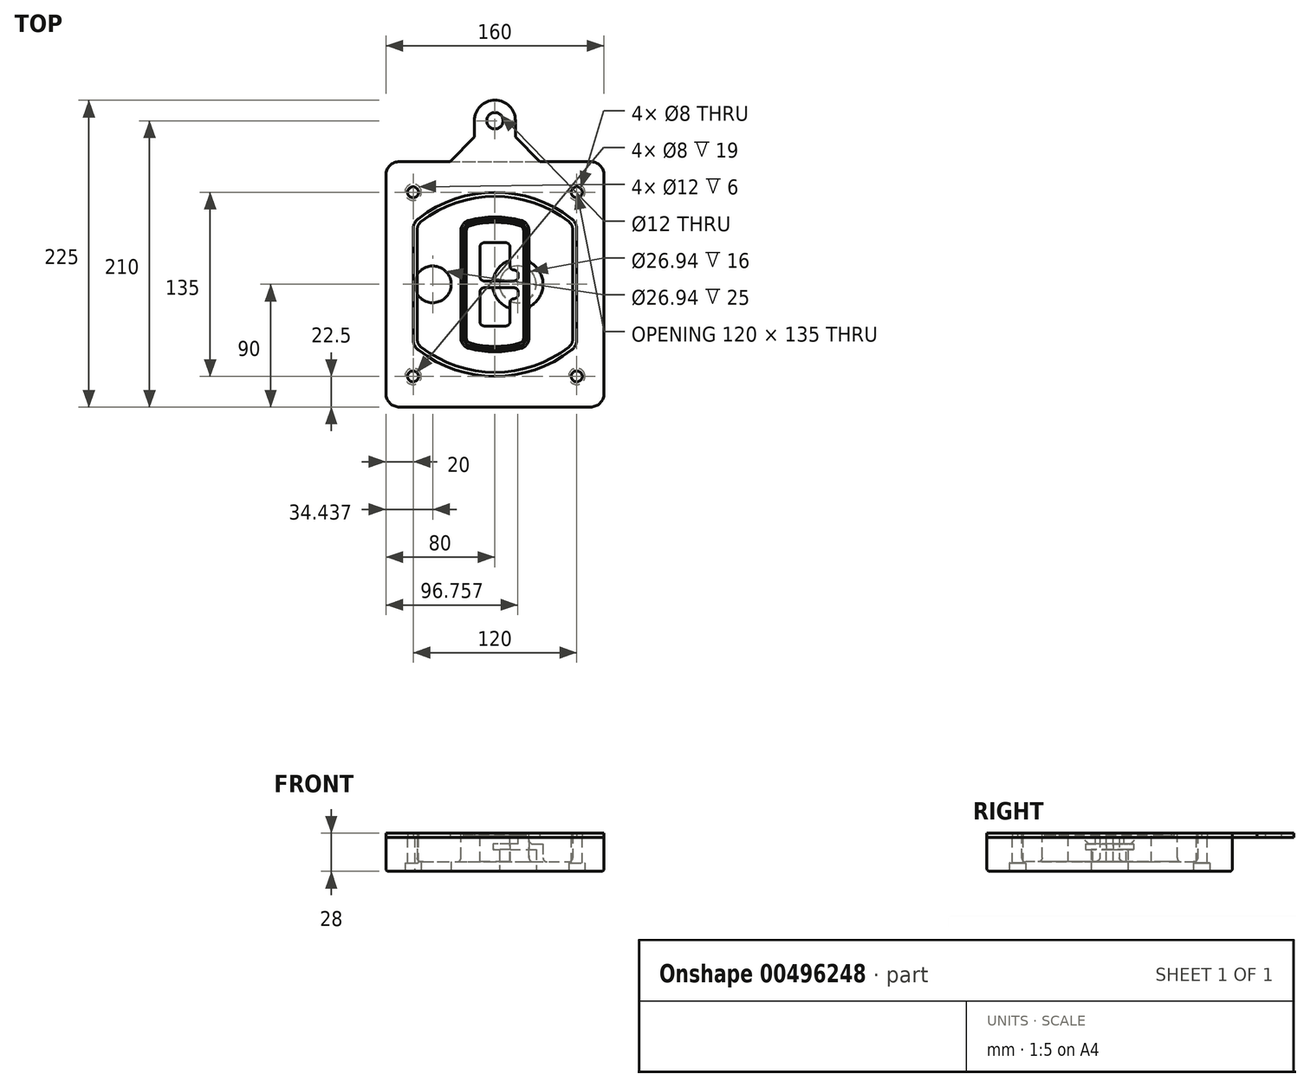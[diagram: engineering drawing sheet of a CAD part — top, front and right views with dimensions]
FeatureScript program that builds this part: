
annotation { "Feature Type Name" : "Feature", "Feature Type Description" : "" }
export const myFeature = defineFeature(function(context is Context, id is Id, definition is map)
    precondition{}
    {
        {
            var Q0;
            Q0=qCreatedBy(makeId("Top.planeOp"),FACE);
            var sketch = newSketch(context, id + "F0", { "sketchPlane" : qUnion([Q0])});
            skPoint(sketch, "E0.rect.middle", {"position": v(0, 0) * mm});
            skLineSegment(sketch, "E1.bottom", {"start": v(-70, -90) * mm, "end": v(70, -90) * mm});
            skLineSegment(sketch, "E1.top", {"start": v(-70, 90) * mm, "end": v(70, 90) * mm});
            skLineSegment(sketch, "E1.left", {"start": v(-80, -80) * mm, "end": v(-80, 80) * mm});
            skLineSegment(sketch, "E1.right", {"start": v(80, -80) * mm, "end": v(80, 80) * mm});
            skLineSegment(sketch, "E2", {"start": v(-80, 90) * mm, "end": v(80, -90) * mm, "construction": true});
            skLineSegment(sketch, "E3", {"start": v(80, 90) * mm, "end": v(-80, -90) * mm, "construction": true});
            skCircle(sketch, "E4", {"center": v(-60, 67.5) * mm, "radius": 4 * mm});
            skCircle(sketch, "E5", {"center": v(60, 67.5) * mm, "radius": 4 * mm});
            skCircle(sketch, "E6", {"center": v(60, -67.5) * mm, "radius": 4 * mm});
            skCircle(sketch, "E7", {"center": v(-60, -67.5) * mm, "radius": 4 * mm});
            skLineSegment(sketch, "E8", {"start": v(-60, 67.5) * mm, "end": v(60, 67.5) * mm, "construction": true});
            skLineSegment(sketch, "E9", {"start": v(60, 67.5) * mm, "end": v(60, -67.5) * mm, "construction": true});
            skLineSegment(sketch, "E10", {"start": v(60, -67.5) * mm, "end": v(-60, -67.5) * mm, "construction": true});
            skLineSegment(sketch, "E11", {"start": v(-60, -67.5) * mm, "end": v(-60, 67.5) * mm, "construction": true});
            skLineSegment(sketch, "E12", {"start": v(-60, 40.3) * mm, "end": v(-60, -40.3) * mm});
            skLineSegment(sketch, "E13", {"start": v(60, 40.3) * mm, "end": v(60, -40.3) * mm});
            skArc(sketch, "E14", {"start": v(56.15, 48.18) * mm, "mid": v(0, 67.5) * mm, "end": v(-56.15, 48.18) * mm});
            skArc(sketch, "E15", {"start": v(-56.15, -48.18) * mm, "mid": v(0, -67.5) * mm, "end": v(56.15, -48.18) * mm});
            skLineSegment(sketch, "E16", {"start": v(-60, 0) * mm, "end": v(60, 0) * mm, "construction": true});
            skPoint(sketch, "E17.visualSharp", {"position": v(-60, -45) * mm});
            skArc(sketch, "E17.filletArc", {"start": v(-60, -40.3) * mm, "mid": v(-58.99, -44.68) * mm, "end": v(-56.15, -48.18) * mm});
            skPoint(sketch, "E18.visualSharp", {"position": v(-60, 45) * mm});
            skArc(sketch, "E18.filletArc", {"start": v(-56.15, 48.18) * mm, "mid": v(-58.99, 44.68) * mm, "end": v(-60, 40.3) * mm});
            skPoint(sketch, "E19.visualSharp", {"position": v(60, 45) * mm});
            skArc(sketch, "E19.filletArc", {"start": v(60, 40.3) * mm, "mid": v(58.99, 44.68) * mm, "end": v(56.15, 48.18) * mm});
            skPoint(sketch, "E20.visualSharp", {"position": v(60, -45) * mm});
            skArc(sketch, "E20.filletArc", {"start": v(56.15, -48.18) * mm, "mid": v(58.99, -44.68) * mm, "end": v(60, -40.3) * mm});
            skPoint(sketch, "E21.visualSharp", {"position": v(-80, 90) * mm});
            skArc(sketch, "E21.filletArc", {"start": v(-70, 90) * mm, "mid": v(-77.07, 87.07) * mm, "end": v(-80, 80) * mm});
            skPoint(sketch, "E22.visualSharp", {"position": v(80, 90) * mm});
            skArc(sketch, "E22.filletArc", {"start": v(80, 80) * mm, "mid": v(77.07, 87.07) * mm, "end": v(70, 90) * mm});
            skPoint(sketch, "E23.visualSharp", {"position": v(80, -90) * mm});
            skArc(sketch, "E23.filletArc", {"start": v(70, -90) * mm, "mid": v(77.07, -87.07) * mm, "end": v(80, -80) * mm});
            skPoint(sketch, "E24.visualSharp", {"position": v(-80, -90) * mm});
            skArc(sketch, "E24.filletArc", {"start": v(-80, -80) * mm, "mid": v(-77.07, -87.07) * mm, "end": v(-70, -90) * mm});
            skArc(sketch, "E25.0", {"start": v(57, 40.3) * mm, "mid": v(56.3, 43.36) * mm, "end": v(54.3, 45.81) * mm});
            skLineSegment(sketch, "E25.1", {"start": v(57, 40.3) * mm, "end": v(57, -40.3) * mm});
            skArc(sketch, "E25.2", {"start": v(54.3, -45.81) * mm, "mid": v(56.3, -43.36) * mm, "end": v(57, -40.3) * mm});
            skArc(sketch, "E25.3", {"start": v(-54.3, -45.81) * mm, "mid": v(0, -64.5) * mm, "end": v(54.3, -45.81) * mm});
            skArc(sketch, "E25.4", {"start": v(-57, -40.3) * mm, "mid": v(-56.3, -43.36) * mm, "end": v(-54.3, -45.81) * mm});
            skArc(sketch, "E25.5", {"start": v(54.3, 45.81) * mm, "mid": v(0, 64.5) * mm, "end": v(-54.3, 45.81) * mm});
            skLineSegment(sketch, "E25.6", {"start": v(-57, 40.3) * mm, "end": v(-57, -40.3) * mm});
            skArc(sketch, "E25.7", {"start": v(-54.3, 45.81) * mm, "mid": v(-56.3, 43.36) * mm, "end": v(-57, 40.3) * mm});
            skArc(sketch, "E26.0", {"start": v(-58.62, 51.33) * mm, "mid": v(-62.58, 46.43) * mm, "end": v(-64, 40.3) * mm});
            skArc(sketch, "E26.1", {"start": v(58.62, 51.33) * mm, "mid": v(0, 71.5) * mm, "end": v(-58.62, 51.33) * mm});
            skArc(sketch, "E26.2", {"start": v(64, 40.3) * mm, "mid": v(62.58, 46.43) * mm, "end": v(58.62, 51.33) * mm});
            skLineSegment(sketch, "E26.3", {"start": v(64, 40.3) * mm, "end": v(64, -40.3) * mm});
            skArc(sketch, "E26.4", {"start": v(58.62, -51.33) * mm, "mid": v(62.58, -46.43) * mm, "end": v(64, -40.3) * mm});
            skLineSegment(sketch, "E26.5", {"start": v(-64, 40.3) * mm, "end": v(-64, -40.3) * mm});
            skArc(sketch, "E26.6", {"start": v(-58.62, -51.33) * mm, "mid": v(0, -71.5) * mm, "end": v(58.62, -51.33) * mm});
            skArc(sketch, "E26.7", {"start": v(-64, -40.3) * mm, "mid": v(-62.58, -46.43) * mm, "end": v(-58.62, -51.33) * mm});
            skSolve(sketch);
        }
        {
            var Q0;
            Q0=makeQuery(id+"F0.imprint","IMPRINT",FACE,{"disambiguationData":[TD([[makeQuery(id+"F0.imprint","IMPRINT",EDGE,{"derivedFrom":sQuery(id+"F0.wireOp",EDGE,"E1.bottom")}),1.0]])]});
            var Q1;
            Q1=makeQuery(id+"F0.imprint","IMPRINT",FACE,{"disambiguationData":[TD([[makeQuery(id+"F0.imprint","IMPRINT",EDGE,{"derivedFrom":sQuery(id+"F0.wireOp",EDGE,"E12")}),1.0]])]});
            var Q2;
            Q2=makeQuery(id+"F0.imprint","IMPRINT",FACE,{"disambiguationData":[TD([[makeQuery(id+"F0.imprint","IMPRINT",EDGE,{"derivedFrom":sQuery(id+"F0.wireOp",EDGE,"E25.0")}),1.0]])]});
            var Q3;
            Q3=makeQuery(id+"F0.imprint","IMPRINT",FACE,{"disambiguationData":[TD([[makeQuery(id+"F0.imprint","IMPRINT",EDGE,{"derivedFrom":sQuery(id+"F0.wireOp",EDGE,"E12")}),-1.0]])]});
            extrude(context, id + "F1", {"entities" : qUnion([Q0, Q1, Q2, Q3]), "oppositeDirection" : true, "depth" : 25 * mm});
        }
        {
            var Q0;
            Q0=makeQuery(id+"F0.imprint","IMPRINT",FACE,{"disambiguationData":[TD([[makeQuery(id+"F0.imprint","IMPRINT",EDGE,{"derivedFrom":sQuery(id+"F0.wireOp",EDGE,"E12")}),1.0]])]});
            extrude(context, id + "F2", {"entities" : qUnion([Q0]), "operationType" : NewBodyOperationType.ADD, "depth" : 3 * mm});
        }
        {
            var Q0;
            Q0=makeQuery(id+"F0.imprint","IMPRINT",FACE,{"disambiguationData":[TD([[makeQuery(id+"F0.imprint","IMPRINT",EDGE,{"derivedFrom":sQuery(id+"F0.wireOp",EDGE,"E25.0")}),1.0]])]});
            extrude(context, id + "F3", {"entities" : qUnion([Q0]), "operationType" : NewBodyOperationType.REMOVE, "oppositeDirection" : true, "depth" : 18 * mm});
        }
        {
            var Q0;
            Q0=makeQuery(id+"F2.opExtrude","CAP_FACE",FACE,{"disambiguationData":[OSD([sQuery(id+"F0.wireOp",EDGE,"E12"),sQuery(id+"F0.wireOp",EDGE,"E13"),sQuery(id+"F0.wireOp",EDGE,"E14"),sQuery(id+"F0.wireOp",EDGE,"E15"),sQuery(id+"F0.wireOp",EDGE,"E17.filletArc"),sQuery(id+"F0.wireOp",EDGE,"E18.filletArc"),sQuery(id+"F0.wireOp",EDGE,"E19.filletArc"),sQuery(id+"F0.wireOp",EDGE,"E20.filletArc"),sQuery(id+"F0.wireOp",EDGE,"E25.0"),sQuery(id+"F0.wireOp",EDGE,"E25.1"),sQuery(id+"F0.wireOp",EDGE,"E25.2"),sQuery(id+"F0.wireOp",EDGE,"E25.3"),sQuery(id+"F0.wireOp",EDGE,"E25.4"),sQuery(id+"F0.wireOp",EDGE,"E25.5"),sQuery(id+"F0.wireOp",EDGE,"E25.6"),sQuery(id+"F0.wireOp",EDGE,"E25.7")])],"isStart":false});
            var sketch = newSketch(context, id + "F4", { "sketchPlane" : qUnion([Q0])});
            skArc(sketch, "E27.0", {"start": v(-19.08, -46.97) * mm, "mid": v(0, -49.5) * mm, "end": v(19.08, -46.97) * mm});
            skArc(sketch, "E28.0", {"start": v(19.08, 46.97) * mm, "mid": v(0, 49.5) * mm, "end": v(-19.08, 46.97) * mm});
            skLineSegment(sketch, "E29", {"start": v(-25, 39.25) * mm, "end": v(-25, -39.25) * mm});
            skLineSegment(sketch, "E30", {"start": v(25, 39.25) * mm, "end": v(25, -39.25) * mm});
            skLineSegment(sketch, "E31", {"start": v(-25, 45.1) * mm, "end": v(25, 45.1) * mm, "construction": true});
            skLineSegment(sketch, "E32", {"start": v(-25, -45.1) * mm, "end": v(25, -45.1) * mm, "construction": true});
            skPoint(sketch, "E33.visualSharp", {"position": v(-25, 45.1) * mm});
            skArc(sketch, "E33.filletArc", {"start": v(-19.08, 46.97) * mm, "mid": v(-23.35, 44.11) * mm, "end": v(-25, 39.25) * mm});
            skPoint(sketch, "E34.visualSharp", {"position": v(25, 45.1) * mm});
            skArc(sketch, "E34.filletArc", {"start": v(25, 39.25) * mm, "mid": v(23.35, 44.11) * mm, "end": v(19.08, 46.97) * mm});
            skPoint(sketch, "E35.visualSharp", {"position": v(25, -45.1) * mm});
            skArc(sketch, "E35.filletArc", {"start": v(19.08, -46.97) * mm, "mid": v(23.35, -44.11) * mm, "end": v(25, -39.25) * mm});
            skPoint(sketch, "E36.visualSharp", {"position": v(-25, -45.1) * mm});
            skArc(sketch, "E36.filletArc", {"start": v(-25, -39.25) * mm, "mid": v(-23.35, -44.11) * mm, "end": v(-19.08, -46.97) * mm});
            skArc(sketch, "E37.0", {"start": v(54.3, 45.81) * mm, "mid": v(0, 64.5) * mm, "end": v(-54.3, 45.81) * mm});
            skArc(sketch, "E37.1", {"start": v(-54.3, 45.81) * mm, "mid": v(-56.3, 43.36) * mm, "end": v(-57, 40.3) * mm});
            skLineSegment(sketch, "E37.2", {"start": v(-57, 40.3) * mm, "end": v(-57, -40.3) * mm});
            skArc(sketch, "E37.3", {"start": v(-57, -40.3) * mm, "mid": v(-56.3, -43.36) * mm, "end": v(-54.3, -45.81) * mm});
            skArc(sketch, "E37.4", {"start": v(-54.3, -45.81) * mm, "mid": v(0, -64.5) * mm, "end": v(54.3, -45.81) * mm});
            skArc(sketch, "E37.5", {"start": v(54.3, -45.81) * mm, "mid": v(56.3, -43.36) * mm, "end": v(57, -40.3) * mm});
            skLineSegment(sketch, "E37.6", {"start": v(57, 40.3) * mm, "end": v(57, -40.3) * mm});
            skArc(sketch, "E37.7", {"start": v(57, 40.3) * mm, "mid": v(56.3, 43.36) * mm, "end": v(54.3, 45.81) * mm});
            skLineSegment(sketch, "E38.0", {"start": v(23, 39.25) * mm, "end": v(23, -39.25) * mm});
            skArc(sketch, "E38.1", {"start": v(18.56, -45.04) * mm, "mid": v(21.76, -42.9) * mm, "end": v(23, -39.25) * mm});
            skArc(sketch, "E38.2", {"start": v(-18.56, -45.04) * mm, "mid": v(0, -47.5) * mm, "end": v(18.56, -45.04) * mm});
            skArc(sketch, "E38.3", {"start": v(-23, -39.25) * mm, "mid": v(-21.76, -42.9) * mm, "end": v(-18.56, -45.04) * mm});
            skLineSegment(sketch, "E38.4", {"start": v(-23, 39.25) * mm, "end": v(-23, -39.25) * mm});
            skArc(sketch, "E38.5", {"start": v(23, 39.25) * mm, "mid": v(21.76, 42.9) * mm, "end": v(18.56, 45.04) * mm});
            skArc(sketch, "E38.6", {"start": v(-18.56, 45.04) * mm, "mid": v(-21.76, 42.9) * mm, "end": v(-23, 39.25) * mm});
            skArc(sketch, "E38.7", {"start": v(18.56, 45.04) * mm, "mid": v(0, 47.5) * mm, "end": v(-18.56, 45.04) * mm});
            skArc(sketch, "E39.0", {"start": v(21, 39.25) * mm, "mid": v(20.18, 41.68) * mm, "end": v(18.04, 43.1) * mm});
            skLineSegment(sketch, "E39.1", {"start": v(21, 39.25) * mm, "end": v(21, -39.25) * mm});
            skArc(sketch, "E39.2", {"start": v(18.04, -43.1) * mm, "mid": v(20.18, -41.68) * mm, "end": v(21, -39.25) * mm});
            skArc(sketch, "E39.3", {"start": v(-18.04, -43.1) * mm, "mid": v(0, -45.5) * mm, "end": v(18.04, -43.1) * mm});
            skArc(sketch, "E39.4", {"start": v(-21, -39.25) * mm, "mid": v(-20.18, -41.68) * mm, "end": v(-18.04, -43.1) * mm});
            skArc(sketch, "E39.5", {"start": v(18.04, 43.1) * mm, "mid": v(0, 45.5) * mm, "end": v(-18.04, 43.1) * mm});
            skLineSegment(sketch, "E39.6", {"start": v(-21, 39.25) * mm, "end": v(-21, -39.25) * mm});
            skArc(sketch, "E39.7", {"start": v(-18.04, 43.1) * mm, "mid": v(-20.18, 41.68) * mm, "end": v(-21, 39.25) * mm});
            skLineSegment(sketch, "E40", {"start": v(-25, 0) * mm, "end": v(25, 0) * mm, "construction": true});
            skLineSegment(sketch, "E41", {"start": v(-11, 5.5) * mm, "end": v(-11, 27.5) * mm});
            skLineSegment(sketch, "E42", {"start": v(-8, 30.5) * mm, "end": v(8, 30.5) * mm});
            skLineSegment(sketch, "E43", {"start": v(11, 27.5) * mm, "end": v(11, 13.5) * mm});
            skLineSegment(sketch, "E44", {"start": v(14, 10.5) * mm, "end": v(14, 10.5) * mm});
            skLineSegment(sketch, "E45", {"start": v(17, 7.5) * mm, "end": v(17, 5.5) * mm});
            skLineSegment(sketch, "E46", {"start": v(14, 2.5) * mm, "end": v(-8, 2.5) * mm});
            skPoint(sketch, "E47.visualSharp", {"position": v(-11, 30.5) * mm});
            skArc(sketch, "E47.filletArc", {"start": v(-8, 30.5) * mm, "mid": v(-10.12, 29.62) * mm, "end": v(-11, 27.5) * mm});
            skPoint(sketch, "E48.visualSharp", {"position": v(11, 30.5) * mm});
            skArc(sketch, "E48.filletArc", {"start": v(11, 27.5) * mm, "mid": v(10.12, 29.62) * mm, "end": v(8, 30.5) * mm});
            skPoint(sketch, "E49.visualSharp", {"position": v(11, 10.5) * mm});
            skArc(sketch, "E49.filletArc", {"start": v(11, 13.5) * mm, "mid": v(11.88, 11.38) * mm, "end": v(14, 10.5) * mm});
            skPoint(sketch, "E50.visualSharp", {"position": v(17, 10.5) * mm});
            skArc(sketch, "E50.filletArc", {"start": v(17, 7.5) * mm, "mid": v(16.12, 9.62) * mm, "end": v(14, 10.5) * mm});
            skPoint(sketch, "E51.visualSharp", {"position": v(17, 2.5) * mm});
            skArc(sketch, "E51.filletArc", {"start": v(14, 2.5) * mm, "mid": v(16.12, 3.38) * mm, "end": v(17, 5.5) * mm});
            skPoint(sketch, "E52.visualSharp", {"position": v(-11, 2.5) * mm});
            skArc(sketch, "E52.filletArc", {"start": v(-11, 5.5) * mm, "mid": v(-10.12, 3.38) * mm, "end": v(-8, 2.5) * mm});
            skLineSegment(sketch, "E53.0.MirrorCS", {"start": v(14, -2.5) * mm, "end": v(-8, -2.5) * mm});
            skArc(sketch, "E54.0.MirrorCS", {"start": v(-11, -5.5) * mm, "mid": v(-10.12, -3.38) * mm, "end": v(-8, -2.5) * mm});
            skLineSegment(sketch, "E55.0.MirrorCS", {"start": v(-11, -5.5) * mm, "end": v(-11, -27.5) * mm});
            skArc(sketch, "E56.0.MirrorCS", {"start": v(-8, -30.5) * mm, "mid": v(-10.12, -29.62) * mm, "end": v(-11, -27.5) * mm});
            skLineSegment(sketch, "E57.0.MirrorCS", {"start": v(-8, -30.5) * mm, "end": v(8, -30.5) * mm});
            skArc(sketch, "E58.0.MirrorCS", {"start": v(11, -27.5) * mm, "mid": v(10.12, -29.62) * mm, "end": v(8, -30.5) * mm});
            skLineSegment(sketch, "E59.0.MirrorCS", {"start": v(11, -27.5) * mm, "end": v(11, -13.5) * mm});
            skArc(sketch, "E60.0.MirrorCS", {"start": v(11, -13.5) * mm, "mid": v(11.88, -11.38) * mm, "end": v(14, -10.5) * mm});
            skArc(sketch, "E61.0.MirrorCS", {"start": v(17, -7.5) * mm, "mid": v(16.12, -9.62) * mm, "end": v(14, -10.5) * mm});
            skLineSegment(sketch, "E62.0.MirrorCS", {"start": v(17, -7.5) * mm, "end": v(17, -5.5) * mm});
            skArc(sketch, "E63.0.MirrorCS", {"start": v(14, -2.5) * mm, "mid": v(16.12, -3.38) * mm, "end": v(17, -5.5) * mm});
            skSolve(sketch);
        }
        {
            var Q0;
            Q0=makeQuery(id+"F4.imprint","IMPRINT",FACE,{"disambiguationData":[TD([[makeQuery(id+"F4.imprint","IMPRINT",EDGE,{"derivedFrom":sQuery(id+"F4.wireOp",EDGE,"E27.0")}),1.0]])]});
            var Q1;
            Q1=makeQuery(id+"F4.imprint","IMPRINT",FACE,{"disambiguationData":[TD([[makeQuery(id+"F4.imprint","IMPRINT",EDGE,{"derivedFrom":sQuery(id+"F4.wireOp",EDGE,"E38.0")}),-1.0]])]});
            var Q2;
            Q2=makeQuery(id+"F4.imprint","IMPRINT",FACE,{"disambiguationData":[TD([[makeQuery(id+"F4.imprint","IMPRINT",EDGE,{"derivedFrom":sQuery(id+"F4.wireOp",EDGE,"E39.0")}),1.0]])]});
            extrude(context, id + "F5", {"entities" : qUnion([Q0, Q1, Q2]), "operationType" : NewBodyOperationType.ADD, "endBound" : BoundingType.UP_TO_NEXT, "oppositeDirection" : true, "depth" : 25 * mm});
        }
        {
            var Q0;
            Q0=makeQuery(id+"F4.imprint","IMPRINT",FACE,{"disambiguationData":[TD([[makeQuery(id+"F4.imprint","IMPRINT",EDGE,{"derivedFrom":sQuery(id+"F4.wireOp",EDGE,"E38.0")}),-1.0]])]});
            extrude(context, id + "F6", {"entities" : qUnion([Q0]), "operationType" : NewBodyOperationType.REMOVE, "oppositeDirection" : true, "depth" : 2 * mm});
        }
        {
            var Q0;
            Q0=makeQuery(id+"F1.opExtrude","CAP_FACE",FACE,{"disambiguationData":[OSD([sQuery(id+"F0.wireOp",EDGE,"E1.bottom"),sQuery(id+"F0.wireOp",EDGE,"E1.top"),sQuery(id+"F0.wireOp",EDGE,"E1.left"),sQuery(id+"F0.wireOp",EDGE,"E1.right"),sQuery(id+"F0.wireOp",EDGE,"E4"),sQuery(id+"F0.wireOp",EDGE,"E5"),sQuery(id+"F0.wireOp",EDGE,"E6"),sQuery(id+"F0.wireOp",EDGE,"E7"),sQuery(id+"F0.wireOp",EDGE,"E21.filletArc"),sQuery(id+"F0.wireOp",EDGE,"E22.filletArc"),sQuery(id+"F0.wireOp",EDGE,"E23.filletArc"),sQuery(id+"F0.wireOp",EDGE,"E24.filletArc")])],"isStart":false});
            var sketch = newSketch(context, id + "F7", { "sketchPlane" : qUnion([Q0])});
            skCircle(sketch, "E64", {"center": v(16.76, 0) * mm, "radius": 13.47 * mm});
            skCircle(sketch, "E65", {"center": v(-45.56, 0) * mm, "radius": 13.47 * mm});
            skLineSegment(sketch, "E66", {"start": v(80, 0) * mm, "end": v(-80, 0) * mm});
            skCircle(sketch, "E67", {"center": v(16.76, 0) * mm, "radius": 18.47 * mm});
            skCircle(sketch, "E68", {"center": v(60, -67.5) * mm, "radius": 6 * mm});
            skCircle(sketch, "E69", {"center": v(-60, -67.5) * mm, "radius": 6 * mm});
            skCircle(sketch, "E70", {"center": v(-60, 67.5) * mm, "radius": 6 * mm});
            skCircle(sketch, "E71", {"center": v(60, 67.5) * mm, "radius": 6 * mm});
            skSolve(sketch);
        }
        {
            var Q0;
            {var subQ1=sQuery(id+"F7.wireOp",EDGE,"E66");var subQ4=sQuery(id+"F7.wireOp",EDGE,"E64");var subQ6=makeQuery(id+"F7.imprint","INTERSECT",VERTEX,{"disambiguationData":[OD(0.0)],"derivedFrom":[subQ4,subQ1]});Q0=makeQuery(id+"F7.imprint","IMPRINT",FACE,{"disambiguationData":[TD([[makeQuery(id+"F7.imprint","IMPRINT",EDGE,{"disambiguationData":[TD([[subQ6,-1.0]])],"derivedFrom":subQ4}),-1.0]])]});}
            var Q1;
            {var subQ0=sQuery(id+"F7.wireOp",EDGE,"E66");var subQ1=sQuery(id+"F7.wireOp",EDGE,"E64");var subQ3=makeQuery(id+"F7.imprint","INTERSECT",VERTEX,{"disambiguationData":[OD(0.0)],"derivedFrom":[subQ1,subQ0]});Q1=makeQuery(id+"F7.imprint","IMPRINT",FACE,{"disambiguationData":[TD([[makeQuery(id+"F7.imprint","IMPRINT",EDGE,{"disambiguationData":[TD([[subQ3,-1.0]])],"derivedFrom":subQ1}),1.0]])]});}
            var Q2;
            {var subQ0=sQuery(id+"F7.wireOp",EDGE,"E66");var subQ1=sQuery(id+"F7.wireOp",EDGE,"E64");var subQ3=makeQuery(id+"F7.imprint","INTERSECT",VERTEX,{"disambiguationData":[OD(0.0)],"derivedFrom":[subQ1,subQ0]});Q2=makeQuery(id+"F7.imprint","IMPRINT",FACE,{"disambiguationData":[TD([[makeQuery(id+"F7.imprint","IMPRINT",EDGE,{"disambiguationData":[TD([[subQ3,1.0]])],"derivedFrom":subQ1}),1.0]])]});}
            var Q3;
            {var subQ1=sQuery(id+"F7.wireOp",EDGE,"E66");var subQ4=sQuery(id+"F7.wireOp",EDGE,"E64");var subQ6=makeQuery(id+"F7.imprint","INTERSECT",VERTEX,{"disambiguationData":[OD(0.0)],"derivedFrom":[subQ4,subQ1]});Q3=makeQuery(id+"F7.imprint","IMPRINT",FACE,{"disambiguationData":[TD([[makeQuery(id+"F7.imprint","IMPRINT",EDGE,{"disambiguationData":[TD([[subQ6,1.0]])],"derivedFrom":subQ4}),-1.0]])]});}
            extrude(context, id + "F8", {"entities" : qUnion([Q0, Q1, Q2, Q3]), "operationType" : NewBodyOperationType.ADD, "oppositeDirection" : true, "depth" : 20 * mm});
        }
        {
            var Q0;
            {var subQ0=sQuery(id+"F7.wireOp",EDGE,"E66");var subQ1=sQuery(id+"F7.wireOp",EDGE,"E64");var subQ3=makeQuery(id+"F7.imprint","INTERSECT",VERTEX,{"disambiguationData":[OD(0.0)],"derivedFrom":[subQ1,subQ0]});Q0=makeQuery(id+"F7.imprint","IMPRINT",FACE,{"disambiguationData":[TD([[makeQuery(id+"F7.imprint","IMPRINT",EDGE,{"disambiguationData":[TD([[subQ3,-1.0]])],"derivedFrom":subQ1}),1.0]])]});}
            var Q1;
            {var subQ0=sQuery(id+"F7.wireOp",EDGE,"E66");var subQ1=sQuery(id+"F7.wireOp",EDGE,"E64");var subQ3=makeQuery(id+"F7.imprint","INTERSECT",VERTEX,{"disambiguationData":[OD(0.0)],"derivedFrom":[subQ1,subQ0]});Q1=makeQuery(id+"F7.imprint","IMPRINT",FACE,{"disambiguationData":[TD([[makeQuery(id+"F7.imprint","IMPRINT",EDGE,{"disambiguationData":[TD([[subQ3,1.0]])],"derivedFrom":subQ1}),1.0]])]});}
            extrude(context, id + "F9", {"entities" : qUnion([Q0, Q1]), "operationType" : NewBodyOperationType.REMOVE, "oppositeDirection" : true, "depth" : 16 * mm});
        }
        {
            var Q0;
            {var subQ0=sQuery(id+"F7.wireOp",EDGE,"E66");var subQ1=sQuery(id+"F7.wireOp",EDGE,"E65");var subQ3=makeQuery(id+"F7.imprint","INTERSECT",VERTEX,{"disambiguationData":[OD(0.0)],"derivedFrom":[subQ1,subQ0]});Q0=makeQuery(id+"F7.imprint","IMPRINT",FACE,{"disambiguationData":[TD([[makeQuery(id+"F7.imprint","IMPRINT",EDGE,{"disambiguationData":[TD([[subQ3,-1.0]])],"derivedFrom":subQ1}),1.0]])]});}
            var Q1;
            {var subQ0=sQuery(id+"F7.wireOp",EDGE,"E66");var subQ1=sQuery(id+"F7.wireOp",EDGE,"E65");var subQ3=makeQuery(id+"F7.imprint","INTERSECT",VERTEX,{"disambiguationData":[OD(0.0)],"derivedFrom":[subQ1,subQ0]});Q1=makeQuery(id+"F7.imprint","IMPRINT",FACE,{"disambiguationData":[TD([[makeQuery(id+"F7.imprint","IMPRINT",EDGE,{"disambiguationData":[TD([[subQ3,1.0]])],"derivedFrom":subQ1}),1.0]])]});}
            extrude(context, id + "F10", {"entities" : qUnion([Q0, Q1]), "operationType" : NewBodyOperationType.REMOVE, "oppositeDirection" : true, "depth" : 25 * mm});
        }
        {
            var Q0;
            Q0=makeQuery(id+"F7.imprint","IMPRINT",FACE,{"disambiguationData":[TD([[makeQuery(id+"F7.imprint","IMPRINT",EDGE,{"derivedFrom":sQuery(id+"F7.wireOp",EDGE,"E68")}),1.0]])]});
            var Q1;
            Q1=makeQuery(id+"F7.imprint","IMPRINT",FACE,{"disambiguationData":[TD([[makeQuery(id+"F7.imprint","IMPRINT",EDGE,{"derivedFrom":makeQuery(id+"F1.opExtrude","CAP_EDGE",EDGE,{"disambiguationData":[OSD([sQuery(id+"F0.wireOp",EDGE,"E5")])],"isStart":false})}),-1.0]])]});
            var Q2;
            Q2=makeQuery(id+"F7.imprint","IMPRINT",FACE,{"disambiguationData":[TD([[makeQuery(id+"F7.imprint","IMPRINT",EDGE,{"derivedFrom":sQuery(id+"F7.wireOp",EDGE,"E69")}),1.0]])]});
            var Q3;
            Q3=makeQuery(id+"F7.imprint","IMPRINT",FACE,{"disambiguationData":[TD([[makeQuery(id+"F7.imprint","IMPRINT",EDGE,{"derivedFrom":makeQuery(id+"F1.opExtrude","CAP_EDGE",EDGE,{"disambiguationData":[OSD([sQuery(id+"F0.wireOp",EDGE,"E4")])],"isStart":false})}),-1.0]])]});
            var Q4;
            Q4=makeQuery(id+"F7.imprint","IMPRINT",FACE,{"disambiguationData":[TD([[makeQuery(id+"F7.imprint","IMPRINT",EDGE,{"derivedFrom":sQuery(id+"F7.wireOp",EDGE,"E70")}),1.0]])]});
            var Q5;
            Q5=makeQuery(id+"F7.imprint","IMPRINT",FACE,{"disambiguationData":[TD([[makeQuery(id+"F7.imprint","IMPRINT",EDGE,{"derivedFrom":makeQuery(id+"F1.opExtrude","CAP_EDGE",EDGE,{"disambiguationData":[OSD([sQuery(id+"F0.wireOp",EDGE,"E7")])],"isStart":false})}),-1.0]])]});
            var Q6;
            Q6=makeQuery(id+"F7.imprint","IMPRINT",FACE,{"disambiguationData":[TD([[makeQuery(id+"F7.imprint","IMPRINT",EDGE,{"derivedFrom":sQuery(id+"F7.wireOp",EDGE,"E71")}),1.0]])]});
            var Q7;
            Q7=makeQuery(id+"F7.imprint","IMPRINT",FACE,{"disambiguationData":[TD([[makeQuery(id+"F7.imprint","IMPRINT",EDGE,{"derivedFrom":makeQuery(id+"F1.opExtrude","CAP_EDGE",EDGE,{"disambiguationData":[OSD([sQuery(id+"F0.wireOp",EDGE,"E6")])],"isStart":false})}),-1.0]])]});
            extrude(context, id + "F11", {"entities" : qUnion([Q0, Q1, Q2, Q3, Q4, Q5, Q6, Q7]), "operationType" : NewBodyOperationType.REMOVE, "oppositeDirection" : true, "depth" : 6 * mm});
        }
        {
            var Q0;
            Q0=makeQuery(id+"F9.boolean.opBoolean","COPY",FACE,{"derivedFrom":makeQuery(id+"F9.opExtrude","CAP_FACE",FACE,{"disambiguationData":[OSD([sQuery(id+"F7.wireOp",EDGE,"E64")])],"isStart":false})});
            var sketch = newSketch(context, id + "F12", { "sketchPlane" : qUnion([Q0])});
            skArc(sketch, "E72.0", {"start": v(11, 17.55) * mm, "mid": v(2.57, 11.82) * mm, "end": v(-1.54, 2.5) * mm});
            skArc(sketch, "E72.1", {"start": v(-1.54, -2.5) * mm, "mid": v(2.57, -11.82) * mm, "end": v(11, -17.55) * mm});
            skLineSegment(sketch, "E73", {"start": v(-1.54, -2.5) * mm, "end": v(14, -2.5) * mm});
            skLineSegment(sketch, "E74.0", {"start": v(14, 2.5) * mm, "end": v(-1.54, 2.5) * mm});
            skArc(sketch, "E74.1", {"start": v(14, 2.5) * mm, "mid": v(16.12, 3.38) * mm, "end": v(17, 5.5) * mm});
            skLineSegment(sketch, "E74.2", {"start": v(17, 7.5) * mm, "end": v(17, 5.5) * mm});
            skArc(sketch, "E74.3", {"start": v(17, 7.5) * mm, "mid": v(16.12, 9.62) * mm, "end": v(14, 10.5) * mm});
            skArc(sketch, "E74.4", {"start": v(11, 13.5) * mm, "mid": v(11.88, 11.38) * mm, "end": v(14, 10.5) * mm});
            skLineSegment(sketch, "E74.5", {"start": v(11, 17.55) * mm, "end": v(11, 13.5) * mm});
            skLineSegment(sketch, "E74.7", {"start": v(14, -2.5) * mm, "end": v(-1.54, -2.5) * mm});
            skArc(sketch, "E74.8", {"start": v(14, -2.5) * mm, "mid": v(16.12, -3.38) * mm, "end": v(17, -5.5) * mm});
            skLineSegment(sketch, "E74.9", {"start": v(17, -7.5) * mm, "end": v(17, -5.5) * mm});
            skArc(sketch, "E74.10", {"start": v(17, -7.5) * mm, "mid": v(16.12, -9.62) * mm, "end": v(14, -10.5) * mm});
            skArc(sketch, "E74.11", {"start": v(11, -13.5) * mm, "mid": v(11.88, -11.38) * mm, "end": v(14, -10.5) * mm});
            skLineSegment(sketch, "E74.12", {"start": v(11, -17.55) * mm, "end": v(11, -13.5) * mm});
            skPoint(sketch, "E75.orphan", {"position": v(11, -27.5) * mm});
            skPoint(sketch, "E76.orphan", {"position": v(-8, -2.5) * mm});
            skPoint(sketch, "E77.orphan", {"position": v(-8, 2.5) * mm});
            skPoint(sketch, "E78.orphan", {"position": v(11, 27.5) * mm});
            skSolve(sketch);
        }
        {
            var Q0;
            {var subQ7=sQuery(id+"F12.wireOp",EDGE,"E72.0");var subQ14=sQuery(id+"F12.wireOp",EDGE,"E72.1");var subQ16=sQuery(id+"F12.wireOp",EDGE,"E74.1");var subQ18=sQuery(id+"F12.wireOp",EDGE,"E74.8");Q0=qUnion([makeQuery(id+"F12.imprint","IMPRINT",FACE,{"disambiguationData":[TD([[makeQuery(id+"F12.imprint","IMPRINT",EDGE,{"derivedFrom":subQ7}),1.0]])]}),makeQuery(id+"F12.imprint","IMPRINT",FACE,{"disambiguationData":[TD([[makeQuery(id+"F12.imprint","IMPRINT",EDGE,{"derivedFrom":subQ14}),1.0]])]}),makeQuery(id+"F12.imprint","IMPRINT",FACE,{"disambiguationData":[TD([[makeQuery(id+"F12.imprint","IMPRINT",EDGE,{"derivedFrom":subQ16}),1.0]])]}),makeQuery(id+"F12.imprint","IMPRINT",FACE,{"disambiguationData":[TD([[makeQuery(id+"F12.imprint","IMPRINT",EDGE,{"derivedFrom":subQ18}),-1.0]])]})]);}
            var Q1;
            Q1=makeQuery(id+"F5.boolean.opBoolean","SPLIT",FACE,{"disambiguationData":[TD([makeQuery(id+"F5.opExtrude","SWEPT_FACE",FACE,{"disambiguationData":[OSD([sQuery(id+"F4.wireOp",EDGE,"E41")])]})])],"derivedFrom":makeQuery(id+"F3.boolean.opBoolean","COPY",FACE,{"derivedFrom":makeQuery(id+"F3.opExtrude","CAP_FACE",FACE,{"disambiguationData":[OSD([sQuery(id+"F0.wireOp",EDGE,"E25.0"),sQuery(id+"F0.wireOp",EDGE,"E25.1"),sQuery(id+"F0.wireOp",EDGE,"E25.2"),sQuery(id+"F0.wireOp",EDGE,"E25.3"),sQuery(id+"F0.wireOp",EDGE,"E25.4"),sQuery(id+"F0.wireOp",EDGE,"E25.5"),sQuery(id+"F0.wireOp",EDGE,"E25.6"),sQuery(id+"F0.wireOp",EDGE,"E25.7")])],"isStart":false})})});
            extrude(context, id + "F13", {"entities" : qUnion([Q0]), "operationType" : NewBodyOperationType.REMOVE, "endBound" : BoundingType.UP_TO_SURFACE, "endBoundEntityFace" : qUnion([Q1]), "depth" : 25 * mm});
        }
        {
            var Q0;
            Q0=makeQuery(id+"F3.boolean.opBoolean","COPY",EDGE,{"derivedFrom":makeQuery(id+"F3.opExtrude","CAP_EDGE",EDGE,{"disambiguationData":[OSD([sQuery(id+"F0.wireOp",EDGE,"E25.6")])],"isStart":false})});
            var Q1;
            Q1=makeQuery(id+"F8.boolean.opBoolean","INTERSECT",EDGE,{"derivedFrom":[makeQuery(id+"F5.opExtrude","SWEPT_FACE",FACE,{"disambiguationData":[OSD([sQuery(id+"F4.wireOp",EDGE,"E30")])]}),makeQuery(id+"F8.opExtrude","CAP_FACE",FACE,{"disambiguationData":[OSD([sQuery(id+"F7.wireOp",EDGE,"E67")])],"isStart":false})]});
            var Q2;
            Q2=makeQuery(id+"F8.boolean.opBoolean","INTERSECT",EDGE,{"disambiguationData":[OD(1.0)],"derivedFrom":[makeQuery(id+"F5.opExtrude","SWEPT_FACE",FACE,{"disambiguationData":[OSD([sQuery(id+"F4.wireOp",EDGE,"E30")])]}),makeQuery(id+"F8.opExtrude","SWEPT_FACE",FACE,{"disambiguationData":[OSD([sQuery(id+"F7.wireOp",EDGE,"E67")])]})]});
            var Q3;
            {var subQ0=sQuery(id+"F4.wireOp",EDGE,"E30");Q3=makeQuery(id+"F8.boolean.opBoolean","SPLIT",EDGE,{"disambiguationData":[TD([makeQuery(id+"F5.opExtrude","SWEPT_FACE",FACE,{"disambiguationData":[OSD([sQuery(id+"F4.wireOp",EDGE,"E35.filletArc")])]})])],"derivedFrom":makeQuery(id+"F5.opExtrude","CAP_EDGE",EDGE,{"disambiguationData":[OSD([subQ0])],"isStart":false})});}
            var Q4;
            {var subQ0=sQuery(id+"F0.wireOp",EDGE,"E25.7");var subQ1=sQuery(id+"F0.wireOp",EDGE,"E25.1");var subQ2=sQuery(id+"F0.wireOp",EDGE,"E25.6");var subQ3=sQuery(id+"F0.wireOp",EDGE,"E25.5");var subQ4=sQuery(id+"F0.wireOp",EDGE,"E25.4");var subQ5=sQuery(id+"F0.wireOp",EDGE,"E25.0");var subQ6=sQuery(id+"F0.wireOp",EDGE,"E25.2");var subQ7=sQuery(id+"F0.wireOp",EDGE,"E25.3");Q4=makeQuery(id+"F8.boolean.opBoolean","INTERSECT",EDGE,{"derivedFrom":[makeQuery(id+"F5.boolean.opBoolean","SPLIT",FACE,{"disambiguationData":[TD([makeQuery(id+"F2.opExtrude","SWEPT_FACE",FACE,{"disambiguationData":[OSD([subQ5])]})])],"derivedFrom":makeQuery(id+"F3.boolean.opBoolean","COPY",FACE,{"derivedFrom":makeQuery(id+"F3.opExtrude","CAP_FACE",FACE,{"disambiguationData":[OSD([subQ5,subQ1,subQ6,subQ7,subQ4,subQ3,subQ2,subQ0])],"isStart":false})})}),makeQuery(id+"F8.opExtrude","SWEPT_FACE",FACE,{"disambiguationData":[OSD([sQuery(id+"F7.wireOp",EDGE,"E67")])]})]});}
            var Q5;
            Q5=makeQuery(id+"F8.boolean.opBoolean","INTERSECT",EDGE,{"disambiguationData":[OD(0.0)],"derivedFrom":[makeQuery(id+"F5.opExtrude","SWEPT_FACE",FACE,{"disambiguationData":[OSD([sQuery(id+"F4.wireOp",EDGE,"E30")])]}),makeQuery(id+"F8.opExtrude","SWEPT_FACE",FACE,{"disambiguationData":[OSD([sQuery(id+"F7.wireOp",EDGE,"E67")])]})]});
            fillet(context, id + "F14", {"entities" : qUnion([Q0, Q1, Q2, Q3, Q4, Q5]), "radius" : 3 * mm, "tangentPropagation" : true, "allowEdgeOverflow" : false});
        }
        {
            var Q0;
            Q0=makeQuery(id+"F1.opExtrude","CAP_EDGE",EDGE,{"disambiguationData":[OSD([sQuery(id+"F0.wireOp",EDGE,"E1.bottom")])],"isStart":false});
            fillet(context, id + "F15", {"entities" : qUnion([Q0]), "radius" : 2 * mm, "tangentPropagation" : true, "allowEdgeOverflow" : false});
        }
        {
            var Q0;
            {var subQ0=sQuery(id+"F0.wireOp",EDGE,"E21.filletArc");var subQ1=sQuery(id+"F0.wireOp",EDGE,"E7");var subQ2=sQuery(id+"F0.wireOp",EDGE,"E6");var subQ3=sQuery(id+"F0.wireOp",EDGE,"E5");var subQ4=sQuery(id+"F0.wireOp",EDGE,"E4");var subQ5=sQuery(id+"F0.wireOp",EDGE,"E22.filletArc");var subQ6=sQuery(id+"F0.wireOp",EDGE,"E1.bottom");var subQ7=sQuery(id+"F0.wireOp",EDGE,"E1.right");var subQ8=sQuery(id+"F0.wireOp",EDGE,"E1.top");var subQ9=sQuery(id+"F0.wireOp",EDGE,"E1.left");var subQ10=sQuery(id+"F0.wireOp",EDGE,"E23.filletArc");var subQ11=sQuery(id+"F0.wireOp",EDGE,"E24.filletArc");Q0=makeQuery(id+"F2.boolean.opBoolean","SPLIT",FACE,{"disambiguationData":[TD([makeQuery(id+"F1.opExtrude","SWEPT_FACE",FACE,{"disambiguationData":[OSD([subQ6])]})])],"derivedFrom":makeQuery(id+"F1.opExtrude","CAP_FACE",FACE,{"disambiguationData":[OSD([subQ6,subQ8,subQ9,subQ7,subQ4,subQ3,subQ2,subQ1,subQ0,subQ5,subQ10,subQ11])],"isStart":true})});}
            var sketch = newSketch(context, id + "F16", { "sketchPlane" : qUnion([Q0])});
            skLineSegment(sketch, "E79", {"start": v(0, 90) * mm, "end": v(0, 120) * mm, "construction": true});
            skCircle(sketch, "E80", {"center": v(0, 120) * mm, "radius": 6 * mm});
            skLineSegment(sketch, "E81", {"start": v(-33, 90) * mm, "end": v(-15, 108) * mm});
            skLineSegment(sketch, "E82", {"start": v(-15, 108) * mm, "end": v(-15, 120) * mm});
            skLineSegment(sketch, "E83", {"start": v(33, 90) * mm, "end": v(15, 108) * mm});
            skLineSegment(sketch, "E84", {"start": v(15, 108) * mm, "end": v(15, 120) * mm});
            skArc(sketch, "E85", {"start": v(15, 120) * mm, "mid": v(0, 135) * mm, "end": v(-15, 120) * mm});
            skLineSegment(sketch, "E86", {"start": v(-80, 0) * mm, "end": v(80, 0) * mm, "construction": true});
            skArc(sketch, "E87.MirrorCS", {"start": v(15, -120) * mm, "mid": v(0, -135) * mm, "end": v(-15, -120) * mm});
            skLineSegment(sketch, "E88.MirrorCS", {"start": v(15, -108) * mm, "end": v(15, -120) * mm});
            skLineSegment(sketch, "E89.MirrorCS", {"start": v(33, -90) * mm, "end": v(15, -108) * mm});
            skLineSegment(sketch, "E90.MirrorCS", {"start": v(-15, -108) * mm, "end": v(-15, -120) * mm});
            skLineSegment(sketch, "E91.MirrorCS", {"start": v(-33, -90) * mm, "end": v(-15, -108) * mm});
            skLineSegment(sketch, "E92.MirrorCS", {"start": v(0, -90) * mm, "end": v(0, -120) * mm, "construction": true});
            skCircle(sketch, "E93.MirrorC", {"center": v(0, -120) * mm, "radius": 6 * mm});
            skSolve(sketch);
        }
        {
            var Q0;
            Q0=makeQuery(id+"F16.imprint","IMPRINT",FACE,{"disambiguationData":[TD([[makeQuery(id+"F16.imprint","IMPRINT",EDGE,{"derivedFrom":makeQuery(id+"F1.opExtrude","CAP_EDGE",EDGE,{"disambiguationData":[OSD([sQuery(id+"F0.wireOp",EDGE,"E1.left")])],"isStart":true})}),-1.0]])]});
            var Q1;
            Q1=makeQuery(id+"F16.imprint","IMPRINT",FACE,{"disambiguationData":[TD([[makeQuery(id+"F16.imprint","IMPRINT",EDGE,{"derivedFrom":sQuery(id+"F16.wireOp",EDGE,"E80")}),-1.0]])]});
            var Q2;
            Q2=makeQuery(id+"F16.imprint","IMPRINT",FACE,{"disambiguationData":[TD([[makeQuery(id+"F16.imprint","IMPRINT",EDGE,{"derivedFrom":sQuery(id+"F16.wireOp",EDGE,"E87.MirrorCS")}),-1.0]])]});
            var Q3;
            Q3=makeQuery(id+"F2.opExtrude","CAP_FACE",FACE,{"disambiguationData":[OSD([sQuery(id+"F0.wireOp",EDGE,"E12"),sQuery(id+"F0.wireOp",EDGE,"E13"),sQuery(id+"F0.wireOp",EDGE,"E14"),sQuery(id+"F0.wireOp",EDGE,"E15"),sQuery(id+"F0.wireOp",EDGE,"E17.filletArc"),sQuery(id+"F0.wireOp",EDGE,"E18.filletArc"),sQuery(id+"F0.wireOp",EDGE,"E19.filletArc"),sQuery(id+"F0.wireOp",EDGE,"E20.filletArc"),sQuery(id+"F0.wireOp",EDGE,"E25.0"),sQuery(id+"F0.wireOp",EDGE,"E25.1"),sQuery(id+"F0.wireOp",EDGE,"E25.2"),sQuery(id+"F0.wireOp",EDGE,"E25.3"),sQuery(id+"F0.wireOp",EDGE,"E25.4"),sQuery(id+"F0.wireOp",EDGE,"E25.5"),sQuery(id+"F0.wireOp",EDGE,"E25.6"),sQuery(id+"F0.wireOp",EDGE,"E25.7")])],"isStart":false});
            extrude(context, id + "F17", {"entities" : qUnion([Q0, Q1, Q2]), "endBound" : BoundingType.UP_TO_SURFACE, "endBoundEntityFace" : qUnion([Q3]), "depth" : 25 * mm});
        }
    });
